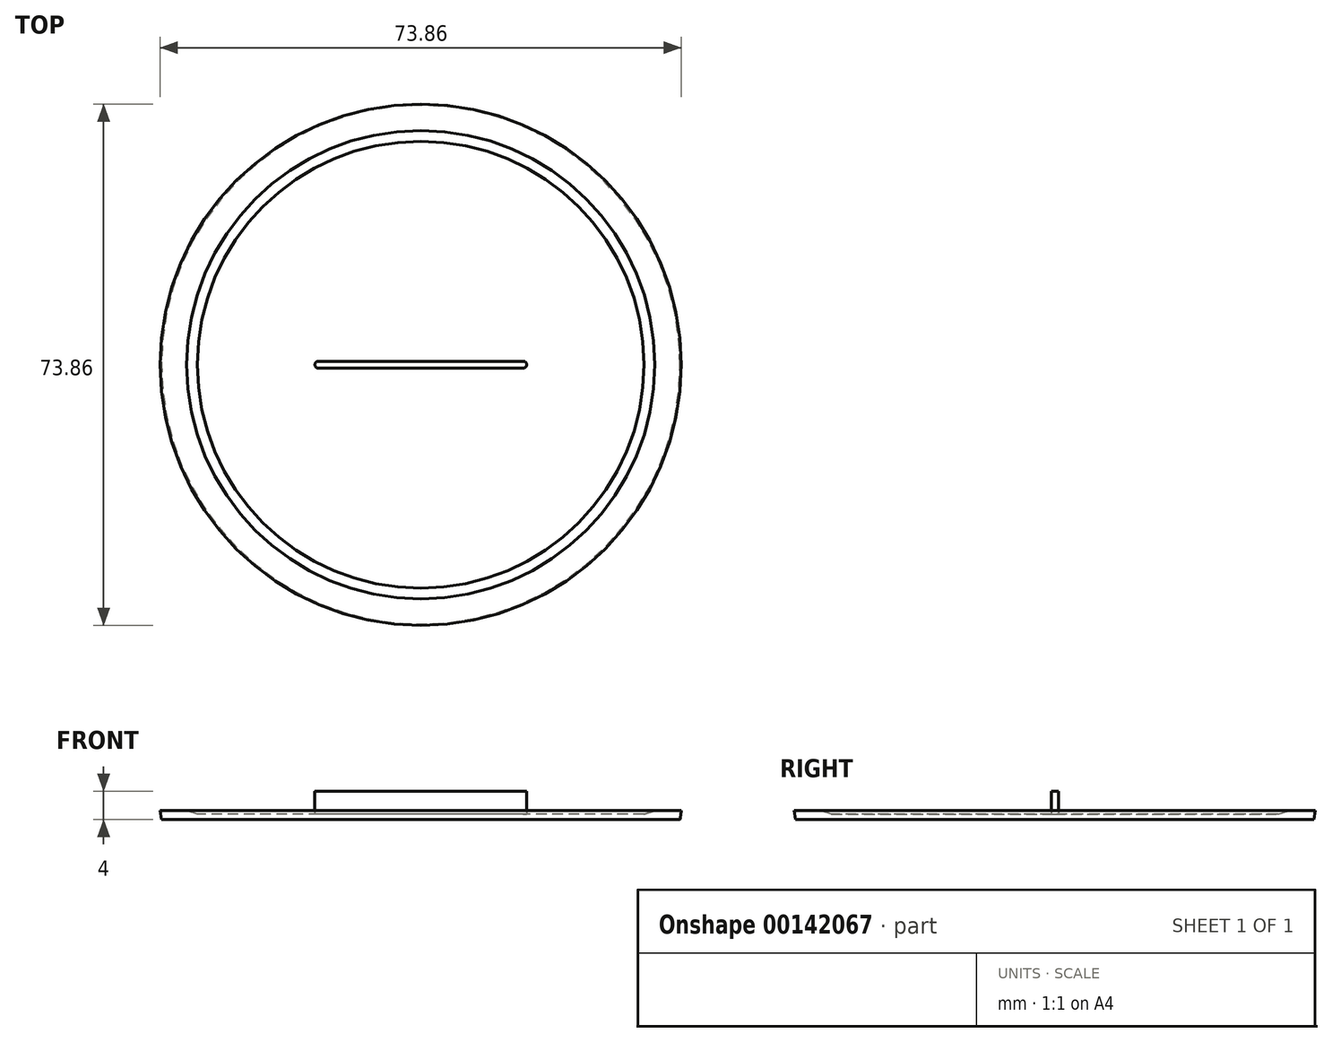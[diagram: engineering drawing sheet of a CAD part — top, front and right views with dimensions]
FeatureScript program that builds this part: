
annotation { "Feature Type Name" : "Feature", "Feature Type Description" : "" }
export const myFeature = defineFeature(function(context is Context, id is Id, definition is map)
    precondition{}
    {
        {
            var Q0;
            Q0=qCreatedBy(makeId("Top.planeOp"),FACE);
            var sketch = newSketch(context, id + "F0", { "sketchPlane" : qUnion([Q0])});
            skCircle(sketch, "E0", {"center": v(0, 0) * mm, "radius": 36.75 * mm});
            skLineSegment(sketch, "E1.bottom", {"start": v(15, -0.5) * mm, "end": v(-15, -0.5) * mm});
            skLineSegment(sketch, "E1.top", {"start": v(15, 0.5) * mm, "end": v(-15, 0.5) * mm});
            skLineSegment(sketch, "E1.left", {"start": v(15, -0.5) * mm, "end": v(15, 0.5) * mm});
            skLineSegment(sketch, "E1.right", {"start": v(-15, -0.5) * mm, "end": v(-15, 0.5) * mm});
            skCircle(sketch, "E2.0", {"center": v(0, 0) * mm, "radius": 31.75 * mm});
            skSolve(sketch);
        }
        {
            var Q0;
            Q0=makeQuery(id+"F0.imprint","IMPRINT",FACE,{"disambiguationData":[TD([[makeQuery(id+"F0.imprint","IMPRINT",EDGE,{"derivedFrom":sQuery(id+"F0.wireOp",EDGE,"E1.bottom")}),1.0]])]});
            extrude(context, id + "F1", {"entities" : qUnion([Q0]), "depth" : .75 * mm});
        }
        {
            var Q0;
            Q0=makeQuery(id+"F0.imprint","IMPRINT",FACE,{"disambiguationData":[TD([[makeQuery(id+"F0.imprint","IMPRINT",EDGE,{"derivedFrom":sQuery(id+"F0.wireOp",EDGE,"E0")}),1.0]])]});
            extrude(context, id + "F2", {"entities" : qUnion([Q0]), "operationType" : NewBodyOperationType.ADD, "depth" : 1.25 * mm, "hasDraft" : true, "draftAngle" : 8 * degree});
        }
        {
            var Q0;
            Q0=makeQuery(id+"F0.imprint","IMPRINT",FACE,{"disambiguationData":[TD([[makeQuery(id+"F0.imprint","IMPRINT",EDGE,{"derivedFrom":sQuery(id+"F0.wireOp",EDGE,"E1.bottom")}),-1.0]])]});
            extrude(context, id + "F3", {"entities" : qUnion([Q0]), "operationType" : NewBodyOperationType.ADD, "depth" : 4 * mm});
        }
        {
            var Q0;
            Q0=makeQuery(id+"F3.opExtrude","SWEPT_EDGE",EDGE,{"disambiguationData":[OSD([sQuery(id+"F0.wireOp",EDGE,"E1.bottom"),sQuery(id+"F0.wireOp",EDGE,"E1.right")])]});
            var Q1;
            Q1=makeQuery(id+"F3.opExtrude","SWEPT_EDGE",EDGE,{"disambiguationData":[OSD([sQuery(id+"F0.wireOp",EDGE,"E1.top"),sQuery(id+"F0.wireOp",EDGE,"E1.right")])]});
            var Q2;
            Q2=makeQuery(id+"F3.opExtrude","SWEPT_EDGE",EDGE,{"disambiguationData":[OSD([sQuery(id+"F0.wireOp",EDGE,"E1.top"),sQuery(id+"F0.wireOp",EDGE,"E1.left")])]});
            var Q3;
            Q3=makeQuery(id+"F3.opExtrude","SWEPT_EDGE",EDGE,{"disambiguationData":[OSD([sQuery(id+"F0.wireOp",EDGE,"E1.bottom"),sQuery(id+"F0.wireOp",EDGE,"E1.left")])]});
            var Q4;
            Q4=makeQuery(id+"F1.opExtrude","CAP_EDGE",EDGE,{"disambiguationData":[OSD([sQuery(id+"F0.wireOp",EDGE,"E1.bottom")])],"isStart":false});
            fillet(context, id + "F4", {"entities" : qUnion([Q0, Q1, Q2, Q3, Q4]), "radius" : .5 * mm, "tangentPropagation" : true, "allowEdgeOverflow" : false});
        }
        {
            var Q0;
            Q0=makeQuery(id+"F2.opExtrude","CAP_EDGE",EDGE,{"disambiguationData":[OSD([sQuery(id+"F0.wireOp",EDGE,"E2.0")])],"isStart":false});
            chamfer(context, id + "F5", {"entities" : qUnion([Q0]), "chamferType" : ChamferType.OFFSET_ANGLE, "width" : .5 * mm, "oppositeDirection" : false, "angle" : 80 * degree, "tangentPropagation" : true});
        }
    });
